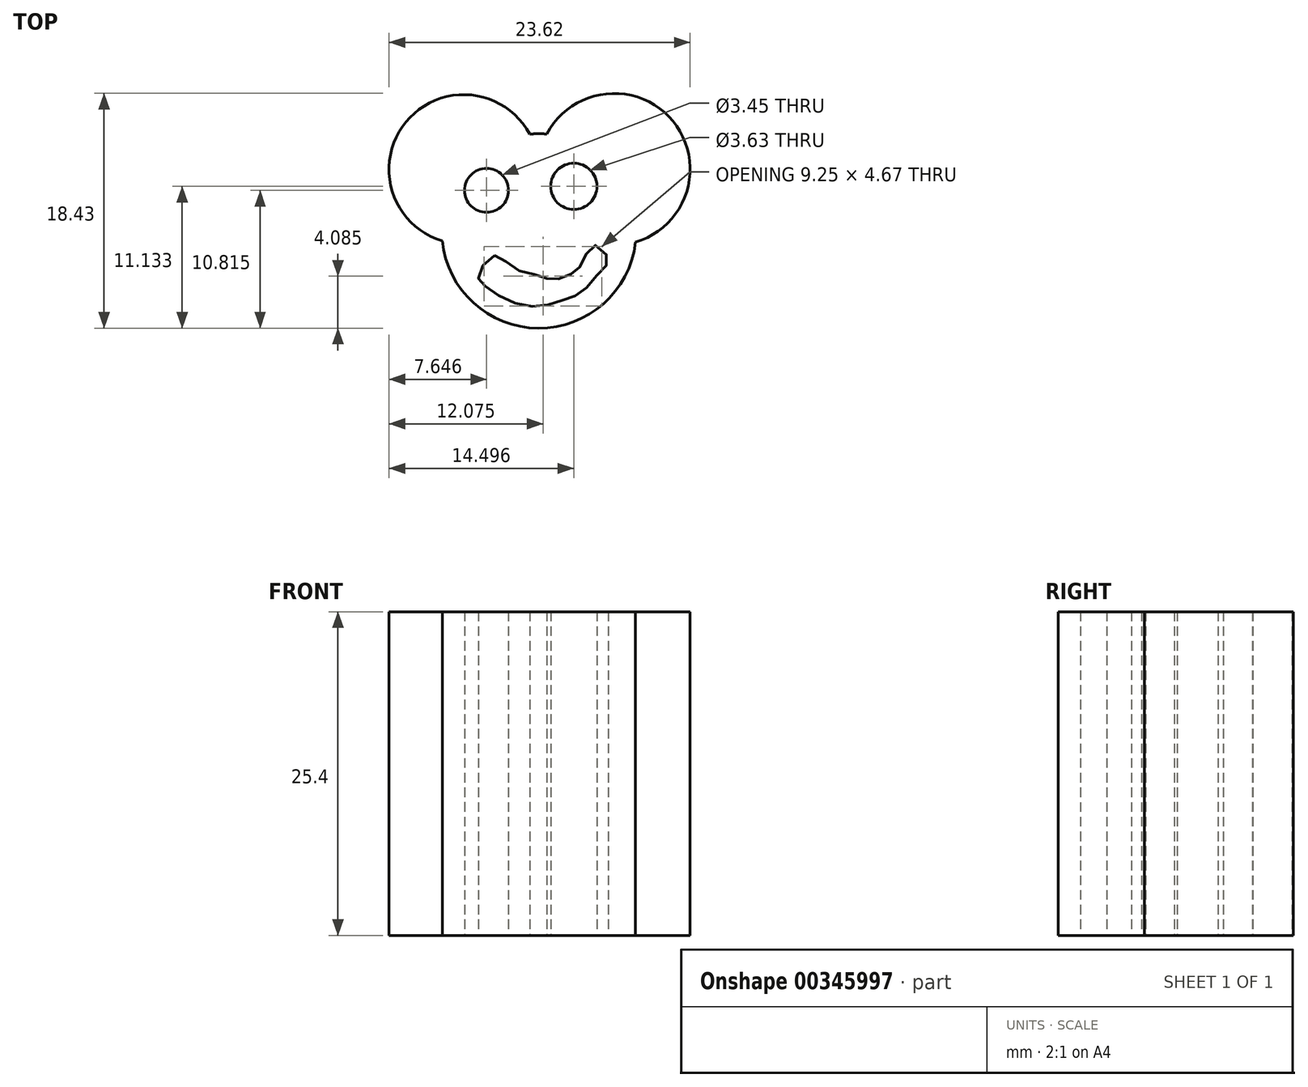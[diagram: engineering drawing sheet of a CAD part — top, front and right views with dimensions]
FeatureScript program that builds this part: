
annotation { "Feature Type Name" : "Feature", "Feature Type Description" : "" }
export const myFeature = defineFeature(function(context is Context, id is Id, definition is map)
    precondition{}
    {
        {
            var Q0;
            Q0=qCreatedBy(makeId("Top.planeOp"),FACE);
            var sketch = newSketch(context, id + "F0", { "sketchPlane" : qUnion([Q0])});
            skLineSegment(sketch, "E0.bottom", {"start": v(-14.15, 16.35) * mm, "end": v(14.52, 16.35) * mm});
            skLineSegment(sketch, "E0.top", {"start": v(-14.15, -39.08) * mm, "end": v(14.52, -39.08) * mm});
            skLineSegment(sketch, "E0.left", {"start": v(-14.15, 16.35) * mm, "end": v(-14.15, -39.08) * mm});
            skLineSegment(sketch, "E0.right", {"start": v(14.52, 16.35) * mm, "end": v(14.52, -39.08) * mm});
            skLineSegment(sketch, "E1", {"start": v(-9.21, 9.66) * mm, "end": v(-9.21, -32.23) * mm});
            skLineSegment(sketch, "E2", {"start": v(-9.21, -32.23) * mm, "end": v(8.95, -32.23) * mm});
            skLineSegment(sketch, "E3", {"start": v(8.95, -32.23) * mm, "end": v(8.95, 10.46) * mm});
            skArc(sketch, "E4", {"start": v(-7.6, 23.22) * mm, "mid": v(-0.05, 16.37) * mm, "end": v(7.58, 23.12) * mm});
            skArc(sketch, "E5.trimOffspring", {"start": v(-0.73, 31.6) * mm, "mid": v(-10.44, 32.55) * mm, "end": v(-7.6, 23.22) * mm});
            skArc(sketch, "E6.trimOffspring", {"start": v(7.58, 23.12) * mm, "mid": v(10.5, 32.61) * mm, "end": v(0.63, 31.6) * mm});
            skArc(sketch, "E7.trimOffspring", {"start": v(0.63, 31.6) * mm, "mid": v(-0.05, 31.63) * mm, "end": v(-0.73, 31.6) * mm});
            skCircle(sketch, "E8", {"center": v(-4.11, 27.18) * mm, "radius": 1.72 * mm});
            skCircle(sketch, "E9", {"center": v(2.74, 27.5) * mm, "radius": 1.82 * mm});
            skFitSpline(sketch, "E10", {"points": [v(-3.48, 22.09) * mm, v(-2.04, 21.13) * mm, v(0, 20.5) * mm, v(1.14, 20.18) * mm, v(2.58, 20.65) * mm, v(3.37, 21.45) * mm, v(4.33, 22.88) * mm, v(5.44, 21.77) * mm, v(4.8, 20.81) * mm, v(3.37, 19.22) * mm, v(1.94, 18.58) * mm, v(0, 18.1) * mm, v(-2.52, 18.58) * mm, v(-4.43, 19.86) * mm, v(-4.75, 20.5) * mm, v(-3.48, 22.09) * mm]});
            skSolve(sketch);
        }
        {
            var Q0;
            Q0=makeQuery(id+"F0.imprint","IMPRINT",FACE,{"disambiguationData":[TD([[makeQuery(id+"F0.imprint","IMPRINT",EDGE,{"derivedFrom":sQuery(id+"F0.wireOp",EDGE,"E4")}),1.0]])]});
            extrude(context, id + "F1", {"entities" : qUnion([Q0]), "depth" : 25.4 * mm});
        }
    });
